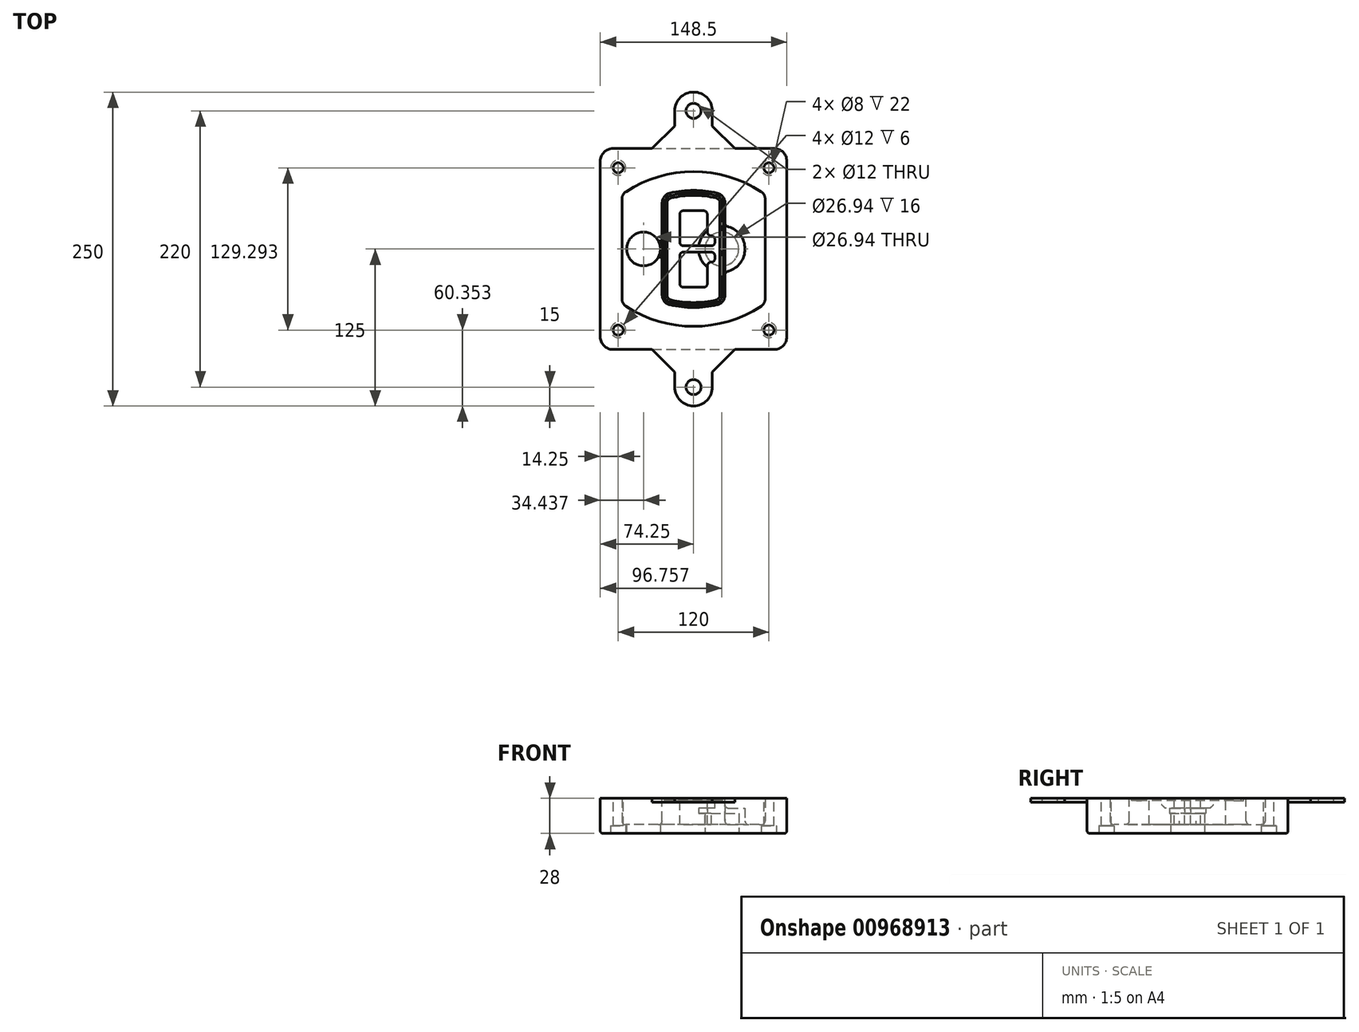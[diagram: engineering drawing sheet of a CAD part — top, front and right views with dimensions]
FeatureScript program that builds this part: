
annotation { "Feature Type Name" : "Feature", "Feature Type Description" : "" }
export const myFeature = defineFeature(function(context is Context, id is Id, definition is map)
    precondition{}
    {
        {
            var Q0;
            Q0=qCreatedBy(makeId("Top.planeOp"),FACE);
            var sketch = newSketch(context, id + "F0", { "sketchPlane" : qUnion([Q0])});
            skPoint(sketch, "E0.rect.middle", {"position": v(0, 0) * mm});
            skLineSegment(sketch, "E1.bottom", {"start": v(-64.25, -80) * mm, "end": v(64.25, -80) * mm});
            skLineSegment(sketch, "E1.top", {"start": v(-64.25, 80) * mm, "end": v(64.25, 80) * mm});
            skLineSegment(sketch, "E1.left", {"start": v(-74.25, -70) * mm, "end": v(-74.25, 70) * mm});
            skLineSegment(sketch, "E1.right", {"start": v(74.25, -70) * mm, "end": v(74.25, 70) * mm});
            skLineSegment(sketch, "E2", {"start": v(-74.25, 80) * mm, "end": v(74.25, -80) * mm, "construction": true});
            skLineSegment(sketch, "E3", {"start": v(74.25, 80) * mm, "end": v(-74.25, -80) * mm, "construction": true});
            skCircle(sketch, "E4", {"center": v(-60, 64.65) * mm, "radius": 4 * mm});
            skCircle(sketch, "E5", {"center": v(60, 64.65) * mm, "radius": 4 * mm});
            skCircle(sketch, "E6", {"center": v(60, -64.65) * mm, "radius": 4 * mm});
            skCircle(sketch, "E7", {"center": v(-60, -64.65) * mm, "radius": 4 * mm});
            skLineSegment(sketch, "E8", {"start": v(-60, 64.65) * mm, "end": v(60, 64.65) * mm, "construction": true});
            skLineSegment(sketch, "E9", {"start": v(60, 64.65) * mm, "end": v(60, -64.65) * mm, "construction": true});
            skLineSegment(sketch, "E10", {"start": v(60, -64.65) * mm, "end": v(-60, -64.65) * mm, "construction": true});
            skLineSegment(sketch, "E11", {"start": v(-60, -64.65) * mm, "end": v(-60, 64.65) * mm, "construction": true});
            skLineSegment(sketch, "E12", {"start": v(-60, 39.77) * mm, "end": v(-60, -39.77) * mm});
            skLineSegment(sketch, "E13", {"start": v(60, 39.77) * mm, "end": v(60, -39.77) * mm});
            skArc(sketch, "E14", {"start": v(55.47, 48.14) * mm, "mid": v(0, 64.65) * mm, "end": v(-55.47, 48.14) * mm});
            skArc(sketch, "E15", {"start": v(-55.47, -48.14) * mm, "mid": v(0, -64.65) * mm, "end": v(55.47, -48.14) * mm});
            skLineSegment(sketch, "E16", {"start": v(-60, 0) * mm, "end": v(60, 0) * mm, "construction": true});
            skPoint(sketch, "E17.visualSharp", {"position": v(-60, -45) * mm});
            skArc(sketch, "E17.filletArc", {"start": v(-60, -39.77) * mm, "mid": v(-58.8, -44.53) * mm, "end": v(-55.47, -48.14) * mm});
            skPoint(sketch, "E18.visualSharp", {"position": v(-60, 45) * mm});
            skArc(sketch, "E18.filletArc", {"start": v(-55.47, 48.14) * mm, "mid": v(-58.8, 44.53) * mm, "end": v(-60, 39.77) * mm});
            skPoint(sketch, "E19.visualSharp", {"position": v(60, 45) * mm});
            skArc(sketch, "E19.filletArc", {"start": v(60, 39.77) * mm, "mid": v(58.8, 44.53) * mm, "end": v(55.47, 48.14) * mm});
            skPoint(sketch, "E20.visualSharp", {"position": v(60, -45) * mm});
            skArc(sketch, "E20.filletArc", {"start": v(55.47, -48.14) * mm, "mid": v(58.8, -44.53) * mm, "end": v(60, -39.77) * mm});
            skPoint(sketch, "E21.visualSharp", {"position": v(-74.25, 80) * mm});
            skArc(sketch, "E21.filletArc", {"start": v(-64.25, 80) * mm, "mid": v(-71.32, 77.07) * mm, "end": v(-74.25, 70) * mm});
            skPoint(sketch, "E22.visualSharp", {"position": v(74.25, 80) * mm});
            skArc(sketch, "E22.filletArc", {"start": v(74.25, 70) * mm, "mid": v(71.32, 77.07) * mm, "end": v(64.25, 80) * mm});
            skPoint(sketch, "E23.visualSharp", {"position": v(74.25, -80) * mm});
            skArc(sketch, "E23.filletArc", {"start": v(64.25, -80) * mm, "mid": v(71.32, -77.07) * mm, "end": v(74.25, -70) * mm});
            skPoint(sketch, "E24.visualSharp", {"position": v(-74.25, -80) * mm});
            skArc(sketch, "E24.filletArc", {"start": v(-74.25, -70) * mm, "mid": v(-71.32, -77.07) * mm, "end": v(-64.25, -80) * mm});
            skArc(sketch, "E25.0", {"start": v(57, 39.77) * mm, "mid": v(56.16, 43.1) * mm, "end": v(53.83, 45.63) * mm});
            skLineSegment(sketch, "E25.1", {"start": v(57, 39.77) * mm, "end": v(57, -39.77) * mm});
            skArc(sketch, "E25.2", {"start": v(53.83, -45.63) * mm, "mid": v(56.16, -43.1) * mm, "end": v(57, -39.77) * mm});
            skArc(sketch, "E25.3", {"start": v(-53.83, -45.63) * mm, "mid": v(0, -61.65) * mm, "end": v(53.83, -45.63) * mm});
            skArc(sketch, "E25.4", {"start": v(-57, -39.77) * mm, "mid": v(-56.16, -43.1) * mm, "end": v(-53.83, -45.63) * mm});
            skArc(sketch, "E25.5", {"start": v(53.83, 45.63) * mm, "mid": v(0, 61.65) * mm, "end": v(-53.83, 45.63) * mm});
            skLineSegment(sketch, "E25.6", {"start": v(-57, 39.77) * mm, "end": v(-57, -39.77) * mm});
            skArc(sketch, "E25.7", {"start": v(-53.83, 45.63) * mm, "mid": v(-56.16, 43.1) * mm, "end": v(-57, 39.77) * mm});
            skArc(sketch, "E26.0", {"start": v(-57.66, 51.49) * mm, "mid": v(-62.31, 46.43) * mm, "end": v(-64, 39.77) * mm});
            skArc(sketch, "E26.1", {"start": v(57.66, 51.49) * mm, "mid": v(0, 68.65) * mm, "end": v(-57.66, 51.49) * mm});
            skArc(sketch, "E26.2", {"start": v(64, 39.77) * mm, "mid": v(62.31, 46.43) * mm, "end": v(57.66, 51.49) * mm});
            skLineSegment(sketch, "E26.3", {"start": v(64, 39.77) * mm, "end": v(64, -39.77) * mm});
            skArc(sketch, "E26.4", {"start": v(57.66, -51.49) * mm, "mid": v(62.31, -46.43) * mm, "end": v(64, -39.77) * mm});
            skLineSegment(sketch, "E26.5", {"start": v(-64, 39.77) * mm, "end": v(-64, -39.77) * mm});
            skArc(sketch, "E26.6", {"start": v(-57.66, -51.49) * mm, "mid": v(0, -68.65) * mm, "end": v(57.66, -51.49) * mm});
            skArc(sketch, "E26.7", {"start": v(-64, -39.77) * mm, "mid": v(-62.31, -46.43) * mm, "end": v(-57.66, -51.49) * mm});
            skSolve(sketch);
        }
        {
            var Q0;
            Q0=makeQuery(id+"F0.imprint","IMPRINT",FACE,{"disambiguationData":[TD([[makeQuery(id+"F0.imprint","IMPRINT",EDGE,{"derivedFrom":sQuery(id+"F0.wireOp",EDGE,"E1.bottom")}),1.0]])]});
            var Q1;
            Q1=makeQuery(id+"F0.imprint","IMPRINT",FACE,{"disambiguationData":[TD([[makeQuery(id+"F0.imprint","IMPRINT",EDGE,{"derivedFrom":sQuery(id+"F0.wireOp",EDGE,"E12")}),1.0]])]});
            var Q2;
            Q2=makeQuery(id+"F0.imprint","IMPRINT",FACE,{"disambiguationData":[TD([[makeQuery(id+"F0.imprint","IMPRINT",EDGE,{"derivedFrom":sQuery(id+"F0.wireOp",EDGE,"E25.0")}),1.0]])]});
            var Q3;
            Q3=makeQuery(id+"F0.imprint","IMPRINT",FACE,{"disambiguationData":[TD([[makeQuery(id+"F0.imprint","IMPRINT",EDGE,{"derivedFrom":sQuery(id+"F0.wireOp",EDGE,"E12")}),-1.0]])]});
            extrude(context, id + "F1", {"entities" : qUnion([Q0, Q1, Q2, Q3]), "oppositeDirection" : true, "depth" : 25 * mm});
        }
        {
            var Q0;
            Q0=makeQuery(id+"F0.imprint","IMPRINT",FACE,{"disambiguationData":[TD([[makeQuery(id+"F0.imprint","IMPRINT",EDGE,{"derivedFrom":sQuery(id+"F0.wireOp",EDGE,"E12")}),1.0]])]});
            extrude(context, id + "F2", {"entities" : qUnion([Q0]), "operationType" : NewBodyOperationType.ADD, "depth" : 3 * mm});
        }
        {
            var Q0;
            Q0=makeQuery(id+"F0.imprint","IMPRINT",FACE,{"disambiguationData":[TD([[makeQuery(id+"F0.imprint","IMPRINT",EDGE,{"derivedFrom":sQuery(id+"F0.wireOp",EDGE,"E25.0")}),1.0]])]});
            extrude(context, id + "F3", {"entities" : qUnion([Q0]), "operationType" : NewBodyOperationType.REMOVE, "oppositeDirection" : true, "depth" : 18 * mm});
        }
        {
            var Q0;
            Q0=makeQuery(id+"F2.opExtrude","CAP_FACE",FACE,{"disambiguationData":[OSD([sQuery(id+"F0.wireOp",EDGE,"E12"),sQuery(id+"F0.wireOp",EDGE,"E13"),sQuery(id+"F0.wireOp",EDGE,"E14"),sQuery(id+"F0.wireOp",EDGE,"E15"),sQuery(id+"F0.wireOp",EDGE,"E17.filletArc"),sQuery(id+"F0.wireOp",EDGE,"E18.filletArc"),sQuery(id+"F0.wireOp",EDGE,"E19.filletArc"),sQuery(id+"F0.wireOp",EDGE,"E20.filletArc"),sQuery(id+"F0.wireOp",EDGE,"E25.0"),sQuery(id+"F0.wireOp",EDGE,"E25.1"),sQuery(id+"F0.wireOp",EDGE,"E25.2"),sQuery(id+"F0.wireOp",EDGE,"E25.3"),sQuery(id+"F0.wireOp",EDGE,"E25.4"),sQuery(id+"F0.wireOp",EDGE,"E25.5"),sQuery(id+"F0.wireOp",EDGE,"E25.6"),sQuery(id+"F0.wireOp",EDGE,"E25.7")])],"isStart":false});
            var sketch = newSketch(context, id + "F4", { "sketchPlane" : qUnion([Q0])});
            skArc(sketch, "E27.0", {"start": v(-18.8, -44.5) * mm, "mid": v(0, -46.65) * mm, "end": v(18.8, -44.5) * mm});
            skArc(sketch, "E28.0", {"start": v(18.8, 44.5) * mm, "mid": v(0, 46.65) * mm, "end": v(-18.8, 44.5) * mm});
            skLineSegment(sketch, "E29", {"start": v(-25, 36.7) * mm, "end": v(-25, -36.7) * mm});
            skLineSegment(sketch, "E30", {"start": v(25, 36.7) * mm, "end": v(25, -36.7) * mm});
            skLineSegment(sketch, "E31", {"start": v(-25, 42.81) * mm, "end": v(25, 42.81) * mm, "construction": true});
            skLineSegment(sketch, "E32", {"start": v(-25, -42.81) * mm, "end": v(25, -42.81) * mm, "construction": true});
            skPoint(sketch, "E33.visualSharp", {"position": v(-25, 42.81) * mm});
            skArc(sketch, "E33.filletArc", {"start": v(-18.8, 44.5) * mm, "mid": v(-23.26, 41.69) * mm, "end": v(-25, 36.7) * mm});
            skPoint(sketch, "E34.visualSharp", {"position": v(25, 42.81) * mm});
            skArc(sketch, "E34.filletArc", {"start": v(25, 36.7) * mm, "mid": v(23.26, 41.69) * mm, "end": v(18.8, 44.5) * mm});
            skPoint(sketch, "E35.visualSharp", {"position": v(25, -42.81) * mm});
            skArc(sketch, "E35.filletArc", {"start": v(18.8, -44.5) * mm, "mid": v(23.26, -41.69) * mm, "end": v(25, -36.7) * mm});
            skPoint(sketch, "E36.visualSharp", {"position": v(-25, -42.81) * mm});
            skArc(sketch, "E36.filletArc", {"start": v(-25, -36.7) * mm, "mid": v(-23.26, -41.69) * mm, "end": v(-18.8, -44.5) * mm});
            skArc(sketch, "E37.0", {"start": v(53.83, 45.63) * mm, "mid": v(0, 61.65) * mm, "end": v(-53.83, 45.63) * mm});
            skArc(sketch, "E37.1", {"start": v(-53.83, 45.63) * mm, "mid": v(-56.16, 43.1) * mm, "end": v(-57, 39.77) * mm});
            skLineSegment(sketch, "E37.2", {"start": v(-57, 39.77) * mm, "end": v(-57, -39.77) * mm});
            skArc(sketch, "E37.3", {"start": v(-57, -39.77) * mm, "mid": v(-56.16, -43.1) * mm, "end": v(-53.83, -45.63) * mm});
            skArc(sketch, "E37.4", {"start": v(-53.83, -45.63) * mm, "mid": v(0, -61.65) * mm, "end": v(53.83, -45.63) * mm});
            skArc(sketch, "E37.5", {"start": v(53.83, -45.63) * mm, "mid": v(56.16, -43.1) * mm, "end": v(57, -39.77) * mm});
            skLineSegment(sketch, "E37.6", {"start": v(57, 39.77) * mm, "end": v(57, -39.77) * mm});
            skArc(sketch, "E37.7", {"start": v(57, 39.77) * mm, "mid": v(56.16, 43.1) * mm, "end": v(53.83, 45.63) * mm});
            skLineSegment(sketch, "E38.0", {"start": v(23, 36.7) * mm, "end": v(23, -36.7) * mm});
            skArc(sketch, "E38.1", {"start": v(18.35, -42.55) * mm, "mid": v(21.7, -40.44) * mm, "end": v(23, -36.7) * mm});
            skArc(sketch, "E38.2", {"start": v(-18.35, -42.55) * mm, "mid": v(0, -44.65) * mm, "end": v(18.35, -42.55) * mm});
            skArc(sketch, "E38.3", {"start": v(-23, -36.7) * mm, "mid": v(-21.7, -40.44) * mm, "end": v(-18.35, -42.55) * mm});
            skLineSegment(sketch, "E38.4", {"start": v(-23, 36.7) * mm, "end": v(-23, -36.7) * mm});
            skArc(sketch, "E38.5", {"start": v(23, 36.7) * mm, "mid": v(21.7, 40.44) * mm, "end": v(18.35, 42.55) * mm});
            skArc(sketch, "E38.6", {"start": v(-18.35, 42.55) * mm, "mid": v(-21.7, 40.44) * mm, "end": v(-23, 36.7) * mm});
            skArc(sketch, "E38.7", {"start": v(18.35, 42.55) * mm, "mid": v(0, 44.65) * mm, "end": v(-18.35, 42.55) * mm});
            skArc(sketch, "E39.0", {"start": v(21, 36.7) * mm, "mid": v(20.13, 39.2) * mm, "end": v(17.9, 40.6) * mm});
            skLineSegment(sketch, "E39.1", {"start": v(21, 36.7) * mm, "end": v(21, -36.7) * mm});
            skArc(sketch, "E39.2", {"start": v(17.9, -40.6) * mm, "mid": v(20.13, -39.2) * mm, "end": v(21, -36.7) * mm});
            skArc(sketch, "E39.3", {"start": v(-17.9, -40.6) * mm, "mid": v(0, -42.65) * mm, "end": v(17.9, -40.6) * mm});
            skArc(sketch, "E39.4", {"start": v(-21, -36.7) * mm, "mid": v(-20.13, -39.2) * mm, "end": v(-17.9, -40.6) * mm});
            skArc(sketch, "E39.5", {"start": v(17.9, 40.6) * mm, "mid": v(0, 42.65) * mm, "end": v(-17.9, 40.6) * mm});
            skLineSegment(sketch, "E39.6", {"start": v(-21, 36.7) * mm, "end": v(-21, -36.7) * mm});
            skArc(sketch, "E39.7", {"start": v(-17.9, 40.6) * mm, "mid": v(-20.13, 39.2) * mm, "end": v(-21, 36.7) * mm});
            skLineSegment(sketch, "E40", {"start": v(-25, 0) * mm, "end": v(25, 0) * mm, "construction": true});
            skLineSegment(sketch, "E41", {"start": v(-11, 5.5) * mm, "end": v(-11, 27.5) * mm});
            skLineSegment(sketch, "E42", {"start": v(-8, 30.5) * mm, "end": v(8, 30.5) * mm});
            skLineSegment(sketch, "E43", {"start": v(11, 27.5) * mm, "end": v(11, 13.5) * mm});
            skLineSegment(sketch, "E44", {"start": v(14, 10.5) * mm, "end": v(14, 10.5) * mm});
            skLineSegment(sketch, "E45", {"start": v(17, 7.5) * mm, "end": v(17, 5.5) * mm});
            skLineSegment(sketch, "E46", {"start": v(14, 2.5) * mm, "end": v(-8, 2.5) * mm});
            skPoint(sketch, "E47.visualSharp", {"position": v(-11, 30.5) * mm});
            skArc(sketch, "E47.filletArc", {"start": v(-8, 30.5) * mm, "mid": v(-10.12, 29.62) * mm, "end": v(-11, 27.5) * mm});
            skPoint(sketch, "E48.visualSharp", {"position": v(11, 30.5) * mm});
            skArc(sketch, "E48.filletArc", {"start": v(11, 27.5) * mm, "mid": v(10.12, 29.62) * mm, "end": v(8, 30.5) * mm});
            skPoint(sketch, "E49.visualSharp", {"position": v(11, 10.5) * mm});
            skArc(sketch, "E49.filletArc", {"start": v(11, 13.5) * mm, "mid": v(11.88, 11.38) * mm, "end": v(14, 10.5) * mm});
            skPoint(sketch, "E50.visualSharp", {"position": v(17, 10.5) * mm});
            skArc(sketch, "E50.filletArc", {"start": v(17, 7.5) * mm, "mid": v(16.12, 9.62) * mm, "end": v(14, 10.5) * mm});
            skPoint(sketch, "E51.visualSharp", {"position": v(17, 2.5) * mm});
            skArc(sketch, "E51.filletArc", {"start": v(14, 2.5) * mm, "mid": v(16.12, 3.38) * mm, "end": v(17, 5.5) * mm});
            skPoint(sketch, "E52.visualSharp", {"position": v(-11, 2.5) * mm});
            skArc(sketch, "E52.filletArc", {"start": v(-11, 5.5) * mm, "mid": v(-10.12, 3.38) * mm, "end": v(-8, 2.5) * mm});
            skLineSegment(sketch, "E53.0.MirrorCS", {"start": v(14, -2.5) * mm, "end": v(-8, -2.5) * mm});
            skArc(sketch, "E54.0.MirrorCS", {"start": v(-11, -5.5) * mm, "mid": v(-10.12, -3.38) * mm, "end": v(-8, -2.5) * mm});
            skLineSegment(sketch, "E55.0.MirrorCS", {"start": v(-11, -5.5) * mm, "end": v(-11, -27.5) * mm});
            skArc(sketch, "E56.0.MirrorCS", {"start": v(-8, -30.5) * mm, "mid": v(-10.12, -29.62) * mm, "end": v(-11, -27.5) * mm});
            skLineSegment(sketch, "E57.0.MirrorCS", {"start": v(-8, -30.5) * mm, "end": v(8, -30.5) * mm});
            skArc(sketch, "E58.0.MirrorCS", {"start": v(11, -27.5) * mm, "mid": v(10.12, -29.62) * mm, "end": v(8, -30.5) * mm});
            skLineSegment(sketch, "E59.0.MirrorCS", {"start": v(11, -27.5) * mm, "end": v(11, -13.5) * mm});
            skArc(sketch, "E60.0.MirrorCS", {"start": v(11, -13.5) * mm, "mid": v(11.88, -11.38) * mm, "end": v(14, -10.5) * mm});
            skArc(sketch, "E61.0.MirrorCS", {"start": v(17, -7.5) * mm, "mid": v(16.12, -9.62) * mm, "end": v(14, -10.5) * mm});
            skLineSegment(sketch, "E62.0.MirrorCS", {"start": v(17, -7.5) * mm, "end": v(17, -5.5) * mm});
            skArc(sketch, "E63.0.MirrorCS", {"start": v(14, -2.5) * mm, "mid": v(16.12, -3.38) * mm, "end": v(17, -5.5) * mm});
            skSolve(sketch);
        }
        {
            var Q0;
            Q0=makeQuery(id+"F4.imprint","IMPRINT",FACE,{"disambiguationData":[TD([[makeQuery(id+"F4.imprint","IMPRINT",EDGE,{"derivedFrom":sQuery(id+"F4.wireOp",EDGE,"E27.0")}),1.0]])]});
            var Q1;
            Q1=makeQuery(id+"F4.imprint","IMPRINT",FACE,{"disambiguationData":[TD([[makeQuery(id+"F4.imprint","IMPRINT",EDGE,{"derivedFrom":sQuery(id+"F4.wireOp",EDGE,"E38.0")}),-1.0]])]});
            var Q2;
            Q2=makeQuery(id+"F4.imprint","IMPRINT",FACE,{"disambiguationData":[TD([[makeQuery(id+"F4.imprint","IMPRINT",EDGE,{"derivedFrom":sQuery(id+"F4.wireOp",EDGE,"E39.0")}),1.0]])]});
            extrude(context, id + "F5", {"entities" : qUnion([Q0, Q1, Q2]), "operationType" : NewBodyOperationType.ADD, "endBound" : BoundingType.UP_TO_NEXT, "oppositeDirection" : true, "depth" : 25 * mm});
        }
        {
            var Q0;
            Q0=makeQuery(id+"F4.imprint","IMPRINT",FACE,{"disambiguationData":[TD([[makeQuery(id+"F4.imprint","IMPRINT",EDGE,{"derivedFrom":sQuery(id+"F4.wireOp",EDGE,"E38.0")}),-1.0]])]});
            extrude(context, id + "F6", {"entities" : qUnion([Q0]), "operationType" : NewBodyOperationType.REMOVE, "oppositeDirection" : true, "depth" : 2 * mm});
        }
        {
            var Q0;
            Q0=makeQuery(id+"F1.opExtrude","CAP_FACE",FACE,{"disambiguationData":[OSD([sQuery(id+"F0.wireOp",EDGE,"E1.bottom"),sQuery(id+"F0.wireOp",EDGE,"E1.top"),sQuery(id+"F0.wireOp",EDGE,"E1.left"),sQuery(id+"F0.wireOp",EDGE,"E1.right"),sQuery(id+"F0.wireOp",EDGE,"E4"),sQuery(id+"F0.wireOp",EDGE,"E5"),sQuery(id+"F0.wireOp",EDGE,"E6"),sQuery(id+"F0.wireOp",EDGE,"E7"),sQuery(id+"F0.wireOp",EDGE,"E21.filletArc"),sQuery(id+"F0.wireOp",EDGE,"E22.filletArc"),sQuery(id+"F0.wireOp",EDGE,"E23.filletArc"),sQuery(id+"F0.wireOp",EDGE,"E24.filletArc")])],"isStart":false});
            var sketch = newSketch(context, id + "F7", { "sketchPlane" : qUnion([Q0])});
            skCircle(sketch, "E64", {"center": v(22.5, 0) * mm, "radius": 13.47 * mm});
            skCircle(sketch, "E65", {"center": v(-39.81, 0) * mm, "radius": 13.47 * mm});
            skLineSegment(sketch, "E66", {"start": v(74.25, 0) * mm, "end": v(-74.25, 0) * mm});
            skCircle(sketch, "E67", {"center": v(22.5, 0) * mm, "radius": 18.47 * mm});
            skCircle(sketch, "E68", {"center": v(60, -64.65) * mm, "radius": 6 * mm});
            skCircle(sketch, "E69", {"center": v(-60, -64.65) * mm, "radius": 6 * mm});
            skCircle(sketch, "E70", {"center": v(-60, 64.65) * mm, "radius": 6 * mm});
            skCircle(sketch, "E71", {"center": v(60, 64.65) * mm, "radius": 6 * mm});
            skSolve(sketch);
        }
        {
            var Q0;
            {var subQ1=sQuery(id+"F7.wireOp",EDGE,"E66");var subQ4=sQuery(id+"F7.wireOp",EDGE,"E64");var subQ6=makeQuery(id+"F7.imprint","INTERSECT",VERTEX,{"disambiguationData":[OD(0.0)],"derivedFrom":[subQ4,subQ1]});Q0=makeQuery(id+"F7.imprint","IMPRINT",FACE,{"disambiguationData":[TD([[makeQuery(id+"F7.imprint","IMPRINT",EDGE,{"disambiguationData":[TD([[subQ6,-1.0]])],"derivedFrom":subQ4}),-1.0]])]});}
            var Q1;
            {var subQ0=sQuery(id+"F7.wireOp",EDGE,"E66");var subQ1=sQuery(id+"F7.wireOp",EDGE,"E64");var subQ3=makeQuery(id+"F7.imprint","INTERSECT",VERTEX,{"disambiguationData":[OD(0.0)],"derivedFrom":[subQ1,subQ0]});Q1=makeQuery(id+"F7.imprint","IMPRINT",FACE,{"disambiguationData":[TD([[makeQuery(id+"F7.imprint","IMPRINT",EDGE,{"disambiguationData":[TD([[subQ3,-1.0]])],"derivedFrom":subQ1}),1.0]])]});}
            var Q2;
            {var subQ0=sQuery(id+"F7.wireOp",EDGE,"E66");var subQ1=sQuery(id+"F7.wireOp",EDGE,"E64");var subQ3=makeQuery(id+"F7.imprint","INTERSECT",VERTEX,{"disambiguationData":[OD(0.0)],"derivedFrom":[subQ1,subQ0]});Q2=makeQuery(id+"F7.imprint","IMPRINT",FACE,{"disambiguationData":[TD([[makeQuery(id+"F7.imprint","IMPRINT",EDGE,{"disambiguationData":[TD([[subQ3,1.0]])],"derivedFrom":subQ1}),1.0]])]});}
            var Q3;
            {var subQ1=sQuery(id+"F7.wireOp",EDGE,"E66");var subQ4=sQuery(id+"F7.wireOp",EDGE,"E64");var subQ6=makeQuery(id+"F7.imprint","INTERSECT",VERTEX,{"disambiguationData":[OD(0.0)],"derivedFrom":[subQ4,subQ1]});Q3=makeQuery(id+"F7.imprint","IMPRINT",FACE,{"disambiguationData":[TD([[makeQuery(id+"F7.imprint","IMPRINT",EDGE,{"disambiguationData":[TD([[subQ6,1.0]])],"derivedFrom":subQ4}),-1.0]])]});}
            extrude(context, id + "F8", {"entities" : qUnion([Q0, Q1, Q2, Q3]), "operationType" : NewBodyOperationType.ADD, "oppositeDirection" : true, "depth" : 20 * mm});
        }
        {
            var Q0;
            {var subQ0=sQuery(id+"F7.wireOp",EDGE,"E66");var subQ1=sQuery(id+"F7.wireOp",EDGE,"E64");var subQ3=makeQuery(id+"F7.imprint","INTERSECT",VERTEX,{"disambiguationData":[OD(0.0)],"derivedFrom":[subQ1,subQ0]});Q0=makeQuery(id+"F7.imprint","IMPRINT",FACE,{"disambiguationData":[TD([[makeQuery(id+"F7.imprint","IMPRINT",EDGE,{"disambiguationData":[TD([[subQ3,-1.0]])],"derivedFrom":subQ1}),1.0]])]});}
            var Q1;
            {var subQ0=sQuery(id+"F7.wireOp",EDGE,"E66");var subQ1=sQuery(id+"F7.wireOp",EDGE,"E64");var subQ3=makeQuery(id+"F7.imprint","INTERSECT",VERTEX,{"disambiguationData":[OD(0.0)],"derivedFrom":[subQ1,subQ0]});Q1=makeQuery(id+"F7.imprint","IMPRINT",FACE,{"disambiguationData":[TD([[makeQuery(id+"F7.imprint","IMPRINT",EDGE,{"disambiguationData":[TD([[subQ3,1.0]])],"derivedFrom":subQ1}),1.0]])]});}
            extrude(context, id + "F9", {"entities" : qUnion([Q0, Q1]), "operationType" : NewBodyOperationType.REMOVE, "oppositeDirection" : true, "depth" : 16 * mm});
        }
        {
            var Q0;
            {var subQ0=sQuery(id+"F7.wireOp",EDGE,"E66");var subQ1=sQuery(id+"F7.wireOp",EDGE,"E65");var subQ3=makeQuery(id+"F7.imprint","INTERSECT",VERTEX,{"disambiguationData":[OD(0.0)],"derivedFrom":[subQ1,subQ0]});Q0=makeQuery(id+"F7.imprint","IMPRINT",FACE,{"disambiguationData":[TD([[makeQuery(id+"F7.imprint","IMPRINT",EDGE,{"disambiguationData":[TD([[subQ3,-1.0]])],"derivedFrom":subQ1}),1.0]])]});}
            var Q1;
            {var subQ0=sQuery(id+"F7.wireOp",EDGE,"E66");var subQ1=sQuery(id+"F7.wireOp",EDGE,"E65");var subQ3=makeQuery(id+"F7.imprint","INTERSECT",VERTEX,{"disambiguationData":[OD(0.0)],"derivedFrom":[subQ1,subQ0]});Q1=makeQuery(id+"F7.imprint","IMPRINT",FACE,{"disambiguationData":[TD([[makeQuery(id+"F7.imprint","IMPRINT",EDGE,{"disambiguationData":[TD([[subQ3,1.0]])],"derivedFrom":subQ1}),1.0]])]});}
            extrude(context, id + "F10", {"entities" : qUnion([Q0, Q1]), "operationType" : NewBodyOperationType.REMOVE, "oppositeDirection" : true, "depth" : 25 * mm});
        }
        {
            var Q0;
            Q0=makeQuery(id+"F7.imprint","IMPRINT",FACE,{"disambiguationData":[TD([[makeQuery(id+"F7.imprint","IMPRINT",EDGE,{"derivedFrom":sQuery(id+"F7.wireOp",EDGE,"E68")}),1.0]])]});
            var Q1;
            Q1=makeQuery(id+"F7.imprint","IMPRINT",FACE,{"disambiguationData":[TD([[makeQuery(id+"F7.imprint","IMPRINT",EDGE,{"derivedFrom":makeQuery(id+"F1.opExtrude","CAP_EDGE",EDGE,{"disambiguationData":[OSD([sQuery(id+"F0.wireOp",EDGE,"E5")])],"isStart":false})}),-1.0]])]});
            var Q2;
            Q2=makeQuery(id+"F7.imprint","IMPRINT",FACE,{"disambiguationData":[TD([[makeQuery(id+"F7.imprint","IMPRINT",EDGE,{"derivedFrom":sQuery(id+"F7.wireOp",EDGE,"E69")}),1.0]])]});
            var Q3;
            Q3=makeQuery(id+"F7.imprint","IMPRINT",FACE,{"disambiguationData":[TD([[makeQuery(id+"F7.imprint","IMPRINT",EDGE,{"derivedFrom":makeQuery(id+"F1.opExtrude","CAP_EDGE",EDGE,{"disambiguationData":[OSD([sQuery(id+"F0.wireOp",EDGE,"E4")])],"isStart":false})}),-1.0]])]});
            var Q4;
            Q4=makeQuery(id+"F7.imprint","IMPRINT",FACE,{"disambiguationData":[TD([[makeQuery(id+"F7.imprint","IMPRINT",EDGE,{"derivedFrom":sQuery(id+"F7.wireOp",EDGE,"E70")}),1.0]])]});
            var Q5;
            Q5=makeQuery(id+"F7.imprint","IMPRINT",FACE,{"disambiguationData":[TD([[makeQuery(id+"F7.imprint","IMPRINT",EDGE,{"derivedFrom":makeQuery(id+"F1.opExtrude","CAP_EDGE",EDGE,{"disambiguationData":[OSD([sQuery(id+"F0.wireOp",EDGE,"E7")])],"isStart":false})}),-1.0]])]});
            var Q6;
            Q6=makeQuery(id+"F7.imprint","IMPRINT",FACE,{"disambiguationData":[TD([[makeQuery(id+"F7.imprint","IMPRINT",EDGE,{"derivedFrom":sQuery(id+"F7.wireOp",EDGE,"E71")}),1.0]])]});
            var Q7;
            Q7=makeQuery(id+"F7.imprint","IMPRINT",FACE,{"disambiguationData":[TD([[makeQuery(id+"F7.imprint","IMPRINT",EDGE,{"derivedFrom":makeQuery(id+"F1.opExtrude","CAP_EDGE",EDGE,{"disambiguationData":[OSD([sQuery(id+"F0.wireOp",EDGE,"E6")])],"isStart":false})}),-1.0]])]});
            extrude(context, id + "F11", {"entities" : qUnion([Q0, Q1, Q2, Q3, Q4, Q5, Q6, Q7]), "operationType" : NewBodyOperationType.REMOVE, "oppositeDirection" : true, "depth" : 6 * mm});
        }
        {
            var Q0;
            Q0=makeQuery(id+"F9.boolean.opBoolean","COPY",FACE,{"derivedFrom":makeQuery(id+"F9.opExtrude","CAP_FACE",FACE,{"disambiguationData":[OSD([sQuery(id+"F7.wireOp",EDGE,"E64")])],"isStart":false})});
            var sketch = newSketch(context, id + "F12", { "sketchPlane" : qUnion([Q0])});
            skArc(sketch, "E72.0", {"start": v(11, 14.45) * mm, "mid": v(6.45, 9.13) * mm, "end": v(4.2, 2.5) * mm});
            skArc(sketch, "E72.1", {"start": v(4.2, -2.5) * mm, "mid": v(6.45, -9.13) * mm, "end": v(11, -14.45) * mm});
            skLineSegment(sketch, "E73", {"start": v(4.2, -2.5) * mm, "end": v(14, -2.5) * mm});
            skLineSegment(sketch, "E74.0", {"start": v(14, 2.5) * mm, "end": v(4.2, 2.5) * mm});
            skArc(sketch, "E74.1", {"start": v(14, 2.5) * mm, "mid": v(16.12, 3.38) * mm, "end": v(17, 5.5) * mm});
            skLineSegment(sketch, "E74.2", {"start": v(17, 7.5) * mm, "end": v(17, 5.5) * mm});
            skArc(sketch, "E74.3", {"start": v(17, 7.5) * mm, "mid": v(16.12, 9.62) * mm, "end": v(14, 10.5) * mm});
            skArc(sketch, "E74.4", {"start": v(11, 13.5) * mm, "mid": v(11.88, 11.38) * mm, "end": v(14, 10.5) * mm});
            skLineSegment(sketch, "E74.5", {"start": v(11, 14.45) * mm, "end": v(11, 13.5) * mm});
            skLineSegment(sketch, "E74.7", {"start": v(14, -2.5) * mm, "end": v(4.2, -2.5) * mm});
            skArc(sketch, "E74.8", {"start": v(14, -2.5) * mm, "mid": v(16.12, -3.38) * mm, "end": v(17, -5.5) * mm});
            skLineSegment(sketch, "E74.9", {"start": v(17, -7.5) * mm, "end": v(17, -5.5) * mm});
            skArc(sketch, "E74.10", {"start": v(17, -7.5) * mm, "mid": v(16.12, -9.62) * mm, "end": v(14, -10.5) * mm});
            skArc(sketch, "E74.11", {"start": v(11, -13.5) * mm, "mid": v(11.88, -11.38) * mm, "end": v(14, -10.5) * mm});
            skLineSegment(sketch, "E74.12", {"start": v(11, -14.45) * mm, "end": v(11, -13.5) * mm});
            skPoint(sketch, "E75.orphan", {"position": v(11, -27.5) * mm});
            skPoint(sketch, "E76.orphan", {"position": v(-8, -2.5) * mm});
            skPoint(sketch, "E77.orphan", {"position": v(-8, 2.5) * mm});
            skPoint(sketch, "E78.orphan", {"position": v(11, 27.5) * mm});
            skSolve(sketch);
        }
        {
            var Q0;
            {var subQ7=sQuery(id+"F12.wireOp",EDGE,"E72.0");var subQ14=sQuery(id+"F12.wireOp",EDGE,"E72.1");var subQ16=sQuery(id+"F12.wireOp",EDGE,"E74.1");var subQ18=sQuery(id+"F12.wireOp",EDGE,"E74.8");Q0=qUnion([makeQuery(id+"F12.imprint","IMPRINT",FACE,{"disambiguationData":[TD([[makeQuery(id+"F12.imprint","IMPRINT",EDGE,{"derivedFrom":subQ7}),1.0]])]}),makeQuery(id+"F12.imprint","IMPRINT",FACE,{"disambiguationData":[TD([[makeQuery(id+"F12.imprint","IMPRINT",EDGE,{"derivedFrom":subQ14}),1.0]])]}),makeQuery(id+"F12.imprint","IMPRINT",FACE,{"disambiguationData":[TD([[makeQuery(id+"F12.imprint","IMPRINT",EDGE,{"derivedFrom":subQ16}),1.0]])]}),makeQuery(id+"F12.imprint","IMPRINT",FACE,{"disambiguationData":[TD([[makeQuery(id+"F12.imprint","IMPRINT",EDGE,{"derivedFrom":subQ18}),-1.0]])]})]);}
            var Q1;
            Q1=makeQuery(id+"F5.boolean.opBoolean","SPLIT",FACE,{"disambiguationData":[TD([makeQuery(id+"F5.opExtrude","SWEPT_FACE",FACE,{"disambiguationData":[OSD([sQuery(id+"F4.wireOp",EDGE,"E41")])]})])],"derivedFrom":makeQuery(id+"F3.boolean.opBoolean","COPY",FACE,{"derivedFrom":makeQuery(id+"F3.opExtrude","CAP_FACE",FACE,{"disambiguationData":[OSD([sQuery(id+"F0.wireOp",EDGE,"E25.0"),sQuery(id+"F0.wireOp",EDGE,"E25.1"),sQuery(id+"F0.wireOp",EDGE,"E25.2"),sQuery(id+"F0.wireOp",EDGE,"E25.3"),sQuery(id+"F0.wireOp",EDGE,"E25.4"),sQuery(id+"F0.wireOp",EDGE,"E25.5"),sQuery(id+"F0.wireOp",EDGE,"E25.6"),sQuery(id+"F0.wireOp",EDGE,"E25.7")])],"isStart":false})})});
            extrude(context, id + "F13", {"entities" : qUnion([Q0]), "operationType" : NewBodyOperationType.REMOVE, "endBound" : BoundingType.UP_TO_SURFACE, "endBoundEntityFace" : qUnion([Q1]), "depth" : 25 * mm});
        }
        {
            var Q0;
            Q0=makeQuery(id+"F3.boolean.opBoolean","COPY",EDGE,{"derivedFrom":makeQuery(id+"F3.opExtrude","CAP_EDGE",EDGE,{"disambiguationData":[OSD([sQuery(id+"F0.wireOp",EDGE,"E25.6")])],"isStart":false})});
            var Q1;
            Q1=makeQuery(id+"F8.boolean.opBoolean","INTERSECT",EDGE,{"derivedFrom":[makeQuery(id+"F5.opExtrude","SWEPT_FACE",FACE,{"disambiguationData":[OSD([sQuery(id+"F4.wireOp",EDGE,"E30")])]}),makeQuery(id+"F8.opExtrude","CAP_FACE",FACE,{"disambiguationData":[OSD([sQuery(id+"F7.wireOp",EDGE,"E67")])],"isStart":false})]});
            var Q2;
            Q2=makeQuery(id+"F8.boolean.opBoolean","INTERSECT",EDGE,{"disambiguationData":[OD(1.0)],"derivedFrom":[makeQuery(id+"F5.opExtrude","SWEPT_FACE",FACE,{"disambiguationData":[OSD([sQuery(id+"F4.wireOp",EDGE,"E30")])]}),makeQuery(id+"F8.opExtrude","SWEPT_FACE",FACE,{"disambiguationData":[OSD([sQuery(id+"F7.wireOp",EDGE,"E67")])]})]});
            var Q3;
            {var subQ0=sQuery(id+"F4.wireOp",EDGE,"E30");Q3=makeQuery(id+"F8.boolean.opBoolean","SPLIT",EDGE,{"disambiguationData":[TD([makeQuery(id+"F5.opExtrude","SWEPT_FACE",FACE,{"disambiguationData":[OSD([sQuery(id+"F4.wireOp",EDGE,"E35.filletArc")])]})])],"derivedFrom":makeQuery(id+"F5.opExtrude","CAP_EDGE",EDGE,{"disambiguationData":[OSD([subQ0])],"isStart":false})});}
            var Q4;
            {var subQ0=sQuery(id+"F0.wireOp",EDGE,"E25.7");var subQ1=sQuery(id+"F0.wireOp",EDGE,"E25.1");var subQ2=sQuery(id+"F0.wireOp",EDGE,"E25.6");var subQ3=sQuery(id+"F0.wireOp",EDGE,"E25.5");var subQ4=sQuery(id+"F0.wireOp",EDGE,"E25.4");var subQ5=sQuery(id+"F0.wireOp",EDGE,"E25.0");var subQ6=sQuery(id+"F0.wireOp",EDGE,"E25.2");var subQ7=sQuery(id+"F0.wireOp",EDGE,"E25.3");Q4=makeQuery(id+"F8.boolean.opBoolean","INTERSECT",EDGE,{"derivedFrom":[makeQuery(id+"F5.boolean.opBoolean","SPLIT",FACE,{"disambiguationData":[TD([makeQuery(id+"F2.opExtrude","SWEPT_FACE",FACE,{"disambiguationData":[OSD([subQ5])]})])],"derivedFrom":makeQuery(id+"F3.boolean.opBoolean","COPY",FACE,{"derivedFrom":makeQuery(id+"F3.opExtrude","CAP_FACE",FACE,{"disambiguationData":[OSD([subQ5,subQ1,subQ6,subQ7,subQ4,subQ3,subQ2,subQ0])],"isStart":false})})}),makeQuery(id+"F8.opExtrude","SWEPT_FACE",FACE,{"disambiguationData":[OSD([sQuery(id+"F7.wireOp",EDGE,"E67")])]})]});}
            var Q5;
            Q5=makeQuery(id+"F8.boolean.opBoolean","INTERSECT",EDGE,{"disambiguationData":[OD(0.0)],"derivedFrom":[makeQuery(id+"F5.opExtrude","SWEPT_FACE",FACE,{"disambiguationData":[OSD([sQuery(id+"F4.wireOp",EDGE,"E30")])]}),makeQuery(id+"F8.opExtrude","SWEPT_FACE",FACE,{"disambiguationData":[OSD([sQuery(id+"F7.wireOp",EDGE,"E67")])]})]});
            fillet(context, id + "F14", {"entities" : qUnion([Q0, Q1, Q2, Q3, Q4, Q5]), "radius" : 3 * mm, "tangentPropagation" : true, "allowEdgeOverflow" : false});
        }
        {
            var Q0;
            Q0=makeQuery(id+"F1.opExtrude","CAP_EDGE",EDGE,{"disambiguationData":[OSD([sQuery(id+"F0.wireOp",EDGE,"E1.bottom")])],"isStart":false});
            fillet(context, id + "F15", {"entities" : qUnion([Q0]), "radius" : 2 * mm, "tangentPropagation" : true, "allowEdgeOverflow" : false});
        }
        {
            var Q0;
            {var subQ0=sQuery(id+"F0.wireOp",EDGE,"E21.filletArc");var subQ1=sQuery(id+"F0.wireOp",EDGE,"E7");var subQ2=sQuery(id+"F0.wireOp",EDGE,"E6");var subQ3=sQuery(id+"F0.wireOp",EDGE,"E5");var subQ4=sQuery(id+"F0.wireOp",EDGE,"E4");var subQ5=sQuery(id+"F0.wireOp",EDGE,"E22.filletArc");var subQ6=sQuery(id+"F0.wireOp",EDGE,"E1.bottom");var subQ7=sQuery(id+"F0.wireOp",EDGE,"E1.right");var subQ8=sQuery(id+"F0.wireOp",EDGE,"E1.top");var subQ9=sQuery(id+"F0.wireOp",EDGE,"E1.left");var subQ10=sQuery(id+"F0.wireOp",EDGE,"E23.filletArc");var subQ11=sQuery(id+"F0.wireOp",EDGE,"E24.filletArc");Q0=makeQuery(id+"F2.boolean.opBoolean","SPLIT",FACE,{"disambiguationData":[TD([makeQuery(id+"F1.opExtrude","SWEPT_FACE",FACE,{"disambiguationData":[OSD([subQ6])]})])],"derivedFrom":makeQuery(id+"F1.opExtrude","CAP_FACE",FACE,{"disambiguationData":[OSD([subQ6,subQ8,subQ9,subQ7,subQ4,subQ3,subQ2,subQ1,subQ0,subQ5,subQ10,subQ11])],"isStart":true})});}
            var sketch = newSketch(context, id + "F16", { "sketchPlane" : qUnion([Q0])});
            skLineSegment(sketch, "E79", {"start": v(0, 80) * mm, "end": v(0, 110) * mm, "construction": true});
            skLineSegment(sketch, "E80", {"start": v(-33, 80) * mm, "end": v(-15, 98) * mm});
            skLineSegment(sketch, "E81", {"start": v(-15, 98) * mm, "end": v(-15, 110) * mm});
            skCircle(sketch, "E82", {"center": v(0, 110) * mm, "radius": 6 * mm});
            skLineSegment(sketch, "E83.MirrorCS", {"start": v(15, 98) * mm, "end": v(15, 110) * mm});
            skLineSegment(sketch, "E84.MirrorCS", {"start": v(33, 80) * mm, "end": v(15, 98) * mm});
            skArc(sketch, "E85", {"start": v(15, 110) * mm, "mid": v(0, 125) * mm, "end": v(-15, 110) * mm});
            skLineSegment(sketch, "E86", {"start": v(-74.25, 0) * mm, "end": v(74.25, 0) * mm, "construction": true});
            skLineSegment(sketch, "E87.MirrorCS", {"start": v(-33, -80) * mm, "end": v(-15, -98) * mm});
            skCircle(sketch, "E88.MirrorC", {"center": v(0, -110) * mm, "radius": 6 * mm});
            skArc(sketch, "E89.MirrorCS", {"start": v(15, -110) * mm, "mid": v(0, -125) * mm, "end": v(-15, -110) * mm});
            skLineSegment(sketch, "E90.MirrorCS", {"start": v(15, -98) * mm, "end": v(15, -110) * mm});
            skLineSegment(sketch, "E91.MirrorCS", {"start": v(-15, -98) * mm, "end": v(-15, -110) * mm});
            skLineSegment(sketch, "E92.MirrorCS", {"start": v(0, -80) * mm, "end": v(0, -110) * mm, "construction": true});
            skLineSegment(sketch, "E93.MirrorCS", {"start": v(33, -80) * mm, "end": v(15, -98) * mm});
            skSolve(sketch);
        }
        {
            var Q0;
            {var subQ0=sQuery(id+"F16.wireOp",EDGE,"E87.MirrorCS");Q0=makeQuery(id+"F16.imprint","IMPRINT",FACE,{"disambiguationData":[TD([[makeQuery(id+"F16.imprint","IMPRINT",EDGE,{"derivedFrom":subQ0}),1.0]])]});}
            var Q1;
            {var subQ0=sQuery(id+"F16.wireOp",EDGE,"E80");Q1=makeQuery(id+"F16.imprint","IMPRINT",FACE,{"disambiguationData":[TD([[makeQuery(id+"F16.imprint","IMPRINT",EDGE,{"derivedFrom":subQ0}),-1.0]])]});}
            var Q2;
            Q2=makeQuery(id+"F16.imprint","IMPRINT",FACE,{"disambiguationData":[TD([[makeQuery(id+"F16.imprint","IMPRINT",EDGE,{"derivedFrom":makeQuery(id+"F1.opExtrude","CAP_EDGE",EDGE,{"disambiguationData":[OSD([sQuery(id+"F0.wireOp",EDGE,"E1.left")])],"isStart":true})}),-1.0]])]});
            var Q3;
            Q3=makeQuery(id+"F2.opExtrude","CAP_FACE",FACE,{"disambiguationData":[OSD([sQuery(id+"F0.wireOp",EDGE,"E12"),sQuery(id+"F0.wireOp",EDGE,"E13"),sQuery(id+"F0.wireOp",EDGE,"E14"),sQuery(id+"F0.wireOp",EDGE,"E15"),sQuery(id+"F0.wireOp",EDGE,"E17.filletArc"),sQuery(id+"F0.wireOp",EDGE,"E18.filletArc"),sQuery(id+"F0.wireOp",EDGE,"E19.filletArc"),sQuery(id+"F0.wireOp",EDGE,"E20.filletArc"),sQuery(id+"F0.wireOp",EDGE,"E25.0"),sQuery(id+"F0.wireOp",EDGE,"E25.1"),sQuery(id+"F0.wireOp",EDGE,"E25.2"),sQuery(id+"F0.wireOp",EDGE,"E25.3"),sQuery(id+"F0.wireOp",EDGE,"E25.4"),sQuery(id+"F0.wireOp",EDGE,"E25.5"),sQuery(id+"F0.wireOp",EDGE,"E25.6"),sQuery(id+"F0.wireOp",EDGE,"E25.7")])],"isStart":false});
            extrude(context, id + "F17", {"entities" : qUnion([Q0, Q1, Q2]), "operationType" : NewBodyOperationType.ADD, "endBound" : BoundingType.UP_TO_SURFACE, "depth" : 25 * mm, "endBoundEntityFace" : qUnion([Q3]), "offsetDistance" : 25 * mm});
        }
    });
